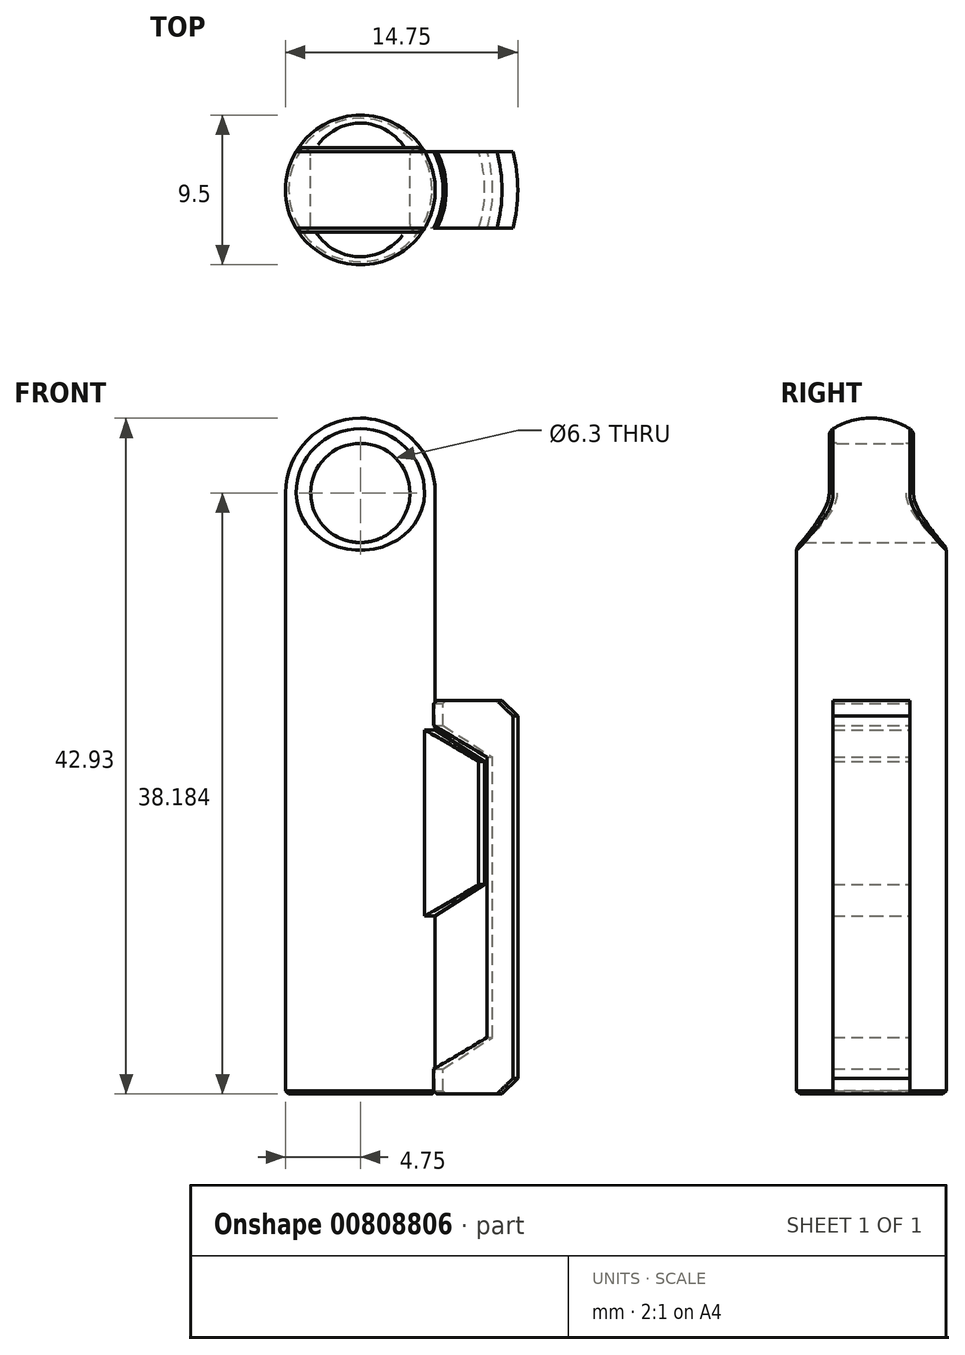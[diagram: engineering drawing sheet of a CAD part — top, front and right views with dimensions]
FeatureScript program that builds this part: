
annotation { "Feature Type Name" : "Feature", "Feature Type Description" : "" }
export const myFeature = defineFeature(function(context is Context, id is Id, definition is map)
    precondition{}
    {
        {
            var Q0;
            Q0=qCreatedBy(makeId("Front.planeOp"),FACE);
            var sketch = newSketch(context, id + "F0", { "sketchPlane" : qUnion([Q0])});
            skLineSegment(sketch, "E0.bottom", {"start": v(0, 34.43) * mm, "end": v(4.75, 34.43) * mm});
            skLineSegment(sketch, "E0.top", {"start": v(5.25, 0) * mm, "end": v(10, 0) * mm});
            skLineSegment(sketch, "E0.left", {"start": v(0, 34.43) * mm, "end": v(0, 0) * mm});
            skLineSegment(sketch, "E0.right", {"start": v(10, 25) * mm, "end": v(10, 0) * mm});
            skLineSegment(sketch, "E1", {"start": v(5.25, 25) * mm, "end": v(5.25, 23.4) * mm});
            skLineSegment(sketch, "E2", {"start": v(5.25, 23.4) * mm, "end": v(8.4, 21.4) * mm});
            skLineSegment(sketch, "E3", {"start": v(8.4, 21.4) * mm, "end": v(8.4, 3.6) * mm});
            skLineSegment(sketch, "E4", {"start": v(8.4, 3.6) * mm, "end": v(5.25, 1.6) * mm});
            skLineSegment(sketch, "E5", {"start": v(5.25, 1.6) * mm, "end": v(5.25, 0) * mm});
            skLineSegment(sketch, "E6", {"start": v(4.75, 34.43) * mm, "end": v(4.75, 23.13) * mm});
            skLineSegment(sketch, "E7", {"start": v(4.75, 23.13) * mm, "end": v(7.9, 21.13) * mm});
            skLineSegment(sketch, "E8", {"start": v(7.9, 21.13) * mm, "end": v(7.9, 13.3) * mm});
            skLineSegment(sketch, "E9", {"start": v(7.9, 13.3) * mm, "end": v(4.75, 11.3) * mm});
            skLineSegment(sketch, "E10.left", {"start": v(0, 0) * mm, "end": v(0, 0) * mm});
            skLineSegment(sketch, "E11", {"start": v(4.75, 0) * mm, "end": v(4.75, 11.3) * mm});
            skLineSegment(sketch, "E12.trimOffspring", {"start": v(5.25, 25) * mm, "end": v(10, 25) * mm});
            skLineSegment(sketch, "E13", {"start": v(0, 0) * mm, "end": v(4.75, 0) * mm});
            skLineSegment(sketch, "E14.bottom", {"start": v(4.75, 34.43) * mm, "end": v(0, 34.43) * mm});
            skLineSegment(sketch, "E14.top", {"start": v(4.75, 38.18) * mm, "end": v(0, 38.18) * mm});
            skLineSegment(sketch, "E14.left", {"start": v(4.75, 34.43) * mm, "end": v(4.75, 38.18) * mm});
            skLineSegment(sketch, "E14.right", {"start": v(0, 34.43) * mm, "end": v(0, 38.18) * mm});
            skArc(sketch, "E15", {"start": v(4.75, 38.18) * mm, "mid": v(3.36, 41.54) * mm, "end": v(0, 42.93) * mm});
            skLineSegment(sketch, "E16", {"start": v(0, 38.18) * mm, "end": v(0, 42.93) * mm});
            skSolve(sketch);
        }
        {
            var Q0;
            {var subQ0=sQuery(id+"F0.wireOp",EDGE,"E0.left");Q0=makeQuery(id+"F0.imprint","IMPRINT",FACE,{"disambiguationData":[TD([[makeQuery(id+"F0.imprint","IMPRINT",EDGE,{"derivedFrom":subQ0}),1.0]])]});}
            var Q1;
            {var subQ1=sQuery(id+"F0.wireOp",EDGE,"E0.right");Q1=makeQuery(id+"F0.imprint","IMPRINT",FACE,{"disambiguationData":[TD([[makeQuery(id+"F0.imprint","IMPRINT",EDGE,{"derivedFrom":subQ1}),-1.0]])]});}
            var Q2;
            Q2=makeQuery(id+"F0.imprint","IMPRINT",FACE,{"disambiguationData":[TD([[makeQuery(id+"F0.imprint","IMPRINT",EDGE,{"derivedFrom":sQuery(id+"F0.wireOp",EDGE,"E0.bottom")}),1.0]])]});
            var Q3;
            Q3=makeQuery(id+"F0.imprint","IMPRINT",FACE,{"disambiguationData":[TD([[makeQuery(id+"F0.imprint","IMPRINT",EDGE,{"derivedFrom":sQuery(id+"F0.wireOp",EDGE,"E14.bottom")}),-1.0]])]});
            var Q4;
            Q4=makeQuery(id+"F0.imprint","IMPRINT",FACE,{"disambiguationData":[TD([[makeQuery(id+"F0.imprint","IMPRINT",EDGE,{"derivedFrom":sQuery(id+"F0.wireOp",EDGE,"E14.top")}),-1.0]])]});
            var Q5;
            Q5=sQuery(id+"F0.wireOp",EDGE,"E0.left");
            revolve(context, id + "F1", {"surfaceOperationType" : NewSurfaceOperationType.NEW, "entities" : qUnion([Q0, Q1, Q2, Q3, Q4]), "axis" : qUnion([Q5]), "revolveType" : RevolveType.FULL});
        }
        {
            var Q0;
            Q0=qCreatedBy(makeId("Front.planeOp"),FACE);
            var sketch = newSketch(context, id + "F2", { "sketchPlane" : qUnion([Q0])});
            skCircle(sketch, "E17", {"center": v(0, 38.18) * mm, "radius": 3.15 * mm});
            skSolve(sketch);
        }
        {
            var Q0;
            Q0=makeQuery(id+"F2.imprint","IMPRINT",FACE,{"disambiguationData":[TD([[makeQuery(id+"F2.imprint","IMPRINT",EDGE,{"derivedFrom":sQuery(id+"F2.wireOp",EDGE,"E17")}),1.0]])]});
            extrude(context, id + "F3", {"entities" : qUnion([Q0]), "operationType" : NewBodyOperationType.REMOVE, "endBound" : BoundingType.SYMMETRIC, "depth" : 25 * mm, "offsetDistance" : 25 * mm});
        }
        {
            var Q0;
            Q0=makeQuery(id+"F1.opRevolve","SWEPT_EDGE",EDGE,{"disambiguationData":[OSD([sQuery(id+"F0.wireOp",EDGE,"E0.right"),sQuery(id+"F0.wireOp",EDGE,"E12.trimOffspring")])]});
            var Q1;
            Q1=makeQuery(id+"F1.opRevolve","SWEPT_EDGE",EDGE,{"disambiguationData":[OSD([sQuery(id+"F0.wireOp",EDGE,"E0.top"),sQuery(id+"F0.wireOp",EDGE,"E0.right")])]});
            chamfer(context, id + "F4", {"entities" : qUnion([Q0, Q1]), "width" : 1 * mm, "tangentPropagation" : true});
        }
        {
            var Q0;
            Q0=makeQuery(id+"F3.boolean.opBoolean","INTERSECT",EDGE,{"disambiguationData":[OD(0.0)],"derivedFrom":[makeQuery(id+"F1.opRevolve","SWEPT_FACE",FACE,{"disambiguationData":[OSD([sQuery(id+"F0.wireOp",EDGE,"E6"),sQuery(id+"F0.wireOp",EDGE,"E14.left")])]}),makeQuery(id+"F3.opExtrude","SWEPT_FACE",FACE,{"disambiguationData":[OSD([sQuery(id+"F2.wireOp",EDGE,"E17")])]})]});
            var Q1;
            Q1=makeQuery(id+"F3.boolean.opBoolean","INTERSECT",EDGE,{"disambiguationData":[OD(0.0)],"derivedFrom":[makeQuery(id+"F1.opRevolve","SWEPT_FACE",FACE,{"disambiguationData":[OSD([sQuery(id+"F0.wireOp",EDGE,"E15")])]}),makeQuery(id+"F3.opExtrude","SWEPT_FACE",FACE,{"disambiguationData":[OSD([sQuery(id+"F2.wireOp",EDGE,"E17")])]})]});
            var Q2;
            Q2=makeQuery(id+"F3.boolean.opBoolean","INTERSECT",EDGE,{"disambiguationData":[OD(1.0)],"derivedFrom":[makeQuery(id+"F1.opRevolve","SWEPT_FACE",FACE,{"disambiguationData":[OSD([sQuery(id+"F0.wireOp",EDGE,"E6"),sQuery(id+"F0.wireOp",EDGE,"E14.left")])]}),makeQuery(id+"F3.opExtrude","SWEPT_FACE",FACE,{"disambiguationData":[OSD([sQuery(id+"F2.wireOp",EDGE,"E17")])]})]});
            var Q3;
            Q3=makeQuery(id+"F3.boolean.opBoolean","INTERSECT",EDGE,{"disambiguationData":[OD(1.0)],"derivedFrom":[makeQuery(id+"F1.opRevolve","SWEPT_FACE",FACE,{"disambiguationData":[OSD([sQuery(id+"F0.wireOp",EDGE,"E15")])]}),makeQuery(id+"F3.opExtrude","SWEPT_FACE",FACE,{"disambiguationData":[OSD([sQuery(id+"F2.wireOp",EDGE,"E17")])]})]});
            fillet(context, id + "F5", {"entities" : qUnion([Q0, Q1, Q2, Q3]), "radius" : 0.5 * mm, "tangentPropagation" : true, "allowEdgeOverflow" : false});
        }
        {
            var Q0;
            Q0=makeQuery(id+"F1.opRevolve","SWEPT_EDGE",EDGE,{"disambiguationData":[OSD([sQuery(id+"F0.wireOp",EDGE,"E11"),sQuery(id+"F0.wireOp",EDGE,"E13")])]});
            var Q1;
            Q1=makeQuery(id+"F1.opRevolve","SWEPT_EDGE",EDGE,{"disambiguationData":[OSD([sQuery(id+"F0.wireOp",EDGE,"E1"),sQuery(id+"F0.wireOp",EDGE,"E12.trimOffspring")])]});
            chamfer(context, id + "F6", {"entities" : qUnion([Q0, Q1]), "width" : 0.2 * mm, "tangentPropagation" : true});
        }
        {
            var Q0;
            Q0=makeQuery(id+"F1.opRevolve","SWEPT_EDGE",EDGE,{"disambiguationData":[OSD([sQuery(id+"F0.wireOp",EDGE,"E0.top"),sQuery(id+"F0.wireOp",EDGE,"E5")])]});
            chamfer(context, id + "F7", {"entities" : qUnion([Q0]), "width" : 0.2 * mm, "tangentPropagation" : true});
        }
        {
            var Q0;
            Q0=qCreatedBy(makeId("Top.planeOp"),FACE);
            var sketch = newSketch(context, id + "F8", { "sketchPlane" : qUnion([Q0])});
            skArc(sketch, "E18.0", {"start": v(4.08, 2.43) * mm, "mid": v(0, 4.75) * mm, "end": v(-4.08, 2.43) * mm});
            skArc(sketch, "E19.0", {"start": v(-4.08, 2.43) * mm, "mid": v(-4.75, 0) * mm, "end": v(-4.08, -2.43) * mm});
            skArc(sketch, "E20.0", {"start": v(4.08, -2.43) * mm, "mid": v(4.75, 0) * mm, "end": v(4.08, 2.43) * mm});
            skArc(sketch, "E21.0", {"start": v(-4.08, -2.43) * mm, "mid": v(0, -4.75) * mm, "end": v(4.08, -2.43) * mm});
            skLineSegment(sketch, "E22", {"start": v(4.08, 2.43) * mm, "end": v(9.75, 2.43) * mm});
            skLineSegment(sketch, "E23", {"start": v(9.75, 2.43) * mm, "end": v(9.75, -2.43) * mm});
            skLineSegment(sketch, "E24", {"start": v(9.75, -2.43) * mm, "end": v(4.08, -2.43) * mm});
            skLineSegment(sketch, "E25.bottom", {"start": v(9.75, 12.95) * mm, "end": v(-17.54, 12.95) * mm});
            skLineSegment(sketch, "E25.top", {"start": v(9.75, -14.22) * mm, "end": v(-17.54, -14.22) * mm});
            skLineSegment(sketch, "E25.left", {"start": v(9.75, 12.95) * mm, "end": v(9.75, -14.22) * mm});
            skLineSegment(sketch, "E25.right", {"start": v(-17.54, 12.95) * mm, "end": v(-17.54, -14.22) * mm});
            skSolve(sketch);
        }
        {
            var Q0;
            Q0=makeQuery(id+"F8.imprint","IMPRINT",FACE,{"disambiguationData":[TD([[makeQuery(id+"F8.imprint","IMPRINT",EDGE,{"derivedFrom":sQuery(id+"F8.wireOp",EDGE,"E18.0")}),-1.0]])]});
            extrude(context, id + "F9", {"entities" : qUnion([Q0]), "operationType" : NewBodyOperationType.REMOVE, "depth" : 25 * mm, "offsetDistance" : 25 * mm});
        }
    });
